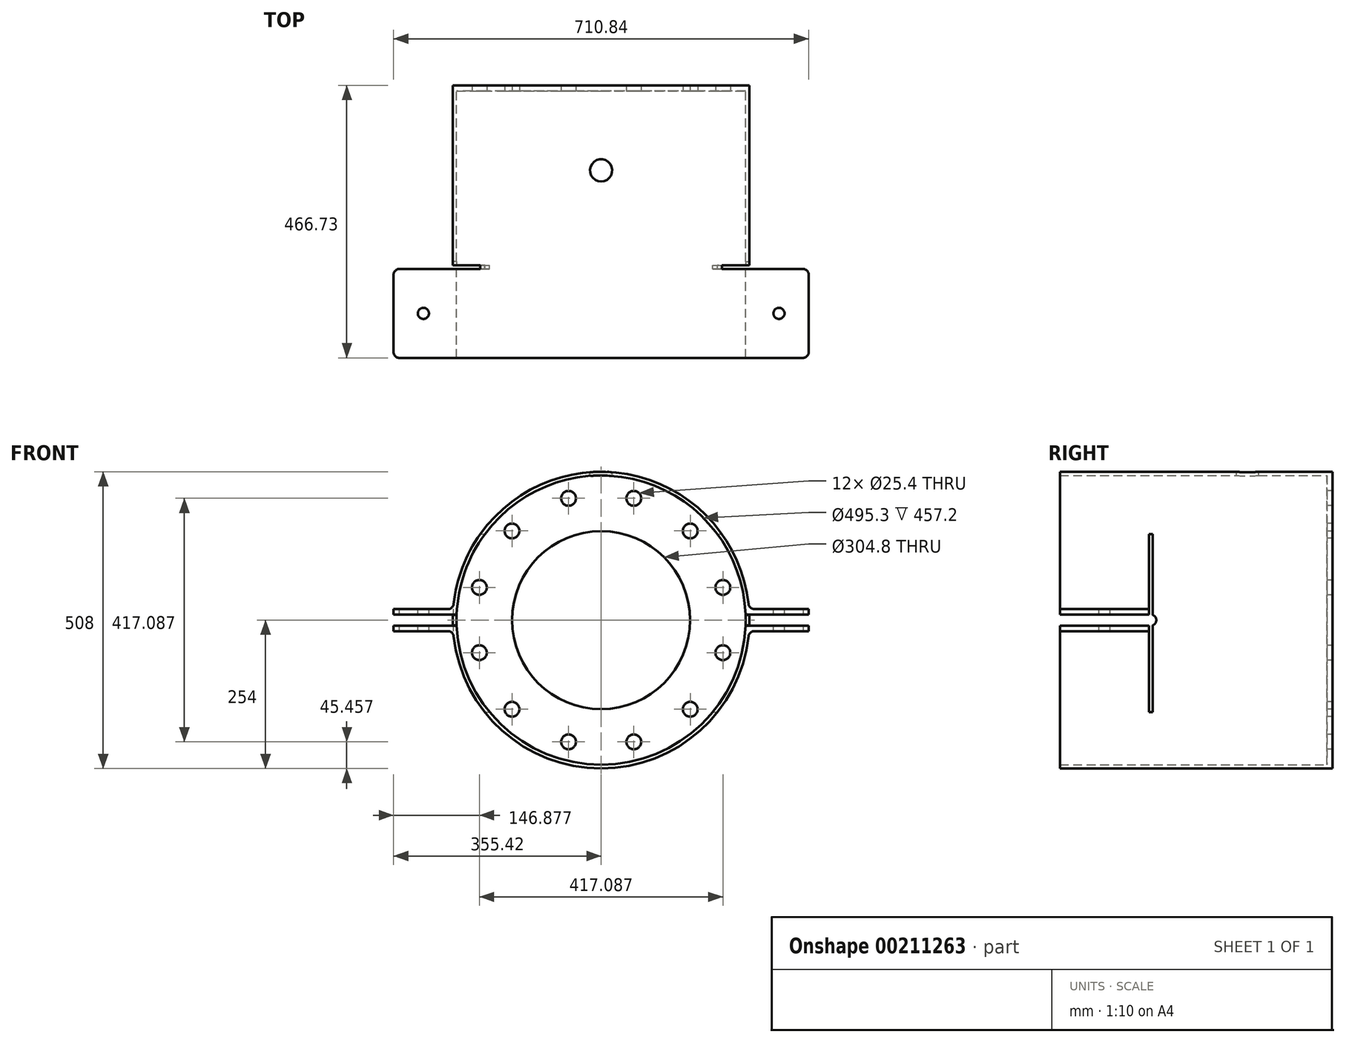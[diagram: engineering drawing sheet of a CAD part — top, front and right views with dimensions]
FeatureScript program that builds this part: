
annotation { "Feature Type Name" : "Feature", "Feature Type Description" : "" }
export const myFeature = defineFeature(function(context is Context, id is Id, definition is map)
    precondition{}
    {
        {
            var Q0;
            Q0=qCreatedBy(makeId("Front.planeOp"),FACE);
            var sketch = newSketch(context, id + "F0", { "sketchPlane" : qUnion([Q0])});
            skCircle(sketch, "E0", {"center": v(0, 0) * mm, "radius": 254 * mm});
            skCircle(sketch, "E1", {"center": v(0, 0) * mm, "radius": 247.65 * mm});
            skSolve(sketch);
        }
        {
            var Q0;
            Q0 = qSketchRegion(id + "F0", true);
            extrude(context, id + "F1", {"entities" : qUnion([Q0]), "depth" : 304.8 * mm});
        }
        {
            var Q0;
            Q0=makeQuery(id+"F1.opExtrude","CAP_FACE",FACE,{"disambiguationData":[OSD([sQuery(id+"F0.wireOp",EDGE,"E0"),sQuery(id+"F0.wireOp",EDGE,"E1")])],"isStart":false});
            var sketch = newSketch(context, id + "F2", { "sketchPlane" : qUnion([Q0])});
            skArc(sketch, "E2", {"start": v(253.82, -9.52) * mm, "mid": v(254, 0) * mm, "end": v(253.82, 9.53) * mm});
            skCircle(sketch, "E3", {"center": v(0, 0) * mm, "radius": 247.65 * mm});
            skLineSegment(sketch, "E4", {"start": v(-253.82, 9.53) * mm, "end": v(-355.42, 9.53) * mm});
            skLineSegment(sketch, "E5", {"start": v(-355.42, 9.53) * mm, "end": v(-355.42, 18.92) * mm});
            skLineSegment(sketch, "E6", {"start": v(-355.42, 18.92) * mm, "end": v(-253.3, 18.92) * mm});
            skLineSegment(sketch, "E7", {"start": v(-253.82, -9.52) * mm, "end": v(-355.42, -9.52) * mm});
            skLineSegment(sketch, "E8", {"start": v(-355.42, -9.52) * mm, "end": v(-355.42, -19.05) * mm});
            skLineSegment(sketch, "E9", {"start": v(-355.42, -19.05) * mm, "end": v(-253.28, -19.05) * mm});
            skLineSegment(sketch, "E10", {"start": v(253.82, 9.53) * mm, "end": v(355.42, 9.53) * mm});
            skLineSegment(sketch, "E11", {"start": v(355.42, 9.53) * mm, "end": v(355.42, 19.05) * mm});
            skLineSegment(sketch, "E12", {"start": v(355.42, 19.05) * mm, "end": v(253.28, 19.05) * mm});
            skLineSegment(sketch, "E13", {"start": v(253.82, -9.52) * mm, "end": v(355.42, -9.52) * mm});
            skLineSegment(sketch, "E14", {"start": v(355.42, -9.52) * mm, "end": v(355.42, -19.05) * mm});
            skLineSegment(sketch, "E15", {"start": v(355.42, -19.05) * mm, "end": v(253.28, -19.05) * mm});
            skArc(sketch, "E16.trimOffspring", {"start": v(253.28, 19.05) * mm, "mid": v(-0.06, 254) * mm, "end": v(-253.3, 18.92) * mm});
            skArc(sketch, "E17.trimOffspring", {"start": v(-253.82, 9.52) * mm, "mid": v(-254, 0) * mm, "end": v(-253.82, -9.53) * mm});
            skArc(sketch, "E18.trimOffspring", {"start": v(-253.28, -19.05) * mm, "mid": v(0, -254) * mm, "end": v(253.28, -19.05) * mm});
            skSolve(sketch);
        }
        {
            var Q0;
            Q0 = qSketchRegion(id + "F2", true);
            extrude(context, id + "F3", {"entities" : qUnion([Q0]), "operationType" : NewBodyOperationType.ADD, "depth" : 152.4 * mm});
        }
        {
            var Q0;
            Q0=makeQuery(id+"F3.opExtrude","CAP_FACE",FACE,{"disambiguationData":[OSD([sQuery(id+"F2.wireOp",EDGE,"E2"),sQuery(id+"F2.wireOp",EDGE,"E3"),sQuery(id+"F2.wireOp",EDGE,"E4"),sQuery(id+"F2.wireOp",EDGE,"E5"),sQuery(id+"F2.wireOp",EDGE,"E6"),sQuery(id+"F2.wireOp",EDGE,"E7"),sQuery(id+"F2.wireOp",EDGE,"E8"),sQuery(id+"F2.wireOp",EDGE,"E9"),sQuery(id+"F2.wireOp",EDGE,"E10"),sQuery(id+"F2.wireOp",EDGE,"E11"),sQuery(id+"F2.wireOp",EDGE,"E12"),sQuery(id+"F2.wireOp",EDGE,"E13"),sQuery(id+"F2.wireOp",EDGE,"E14"),sQuery(id+"F2.wireOp",EDGE,"E15"),sQuery(id+"F2.wireOp",EDGE,"E16.trimOffspring"),sQuery(id+"F2.wireOp",EDGE,"E17.trimOffspring"),sQuery(id+"F2.wireOp",EDGE,"E18.trimOffspring")])],"isStart":false});
            var sketch = newSketch(context, id + "F4", { "sketchPlane" : qUnion([Q0])});
            skLineSegment(sketch, "E19.bottom", {"start": v(-378.58, 9.53) * mm, "end": v(378.58, 9.53) * mm});
            skLineSegment(sketch, "E19.top", {"start": v(-378.58, -9.53) * mm, "end": v(378.58, -9.53) * mm});
            skLineSegment(sketch, "E19.left", {"start": v(-378.58, 9.53) * mm, "end": v(-378.58, -9.53) * mm});
            skLineSegment(sketch, "E19.right", {"start": v(378.58, 9.53) * mm, "end": v(378.58, -9.53) * mm});
            skPoint(sketch, "E19.middle", {"position": v(0, 0) * mm});
            skSolve(sketch);
        }
        {
            var Q0;
            Q0 = qSketchRegion(id + "F4", true);
            extrude(context, id + "F5", {"entities" : qUnion([Q0]), "operationType" : NewBodyOperationType.REMOVE, "oppositeDirection" : true, "depth" : 165.1 * mm});
        }
        {
            var Q0;
            {var subQ0=sQuery(id+"F4.wireOp",EDGE,"E19.bottom");Q0=makeQuery(id+"F5.boolean.opBoolean","COPY",EDGE,{"disambiguationData":[TD([makeQuery(id+"F3.opExtrude","SWEPT_FACE",FACE,{"disambiguationData":[OSD([sQuery(id+"F2.wireOp",EDGE,"E4")])]})])],"derivedFrom":makeQuery(id+"F5.opExtrude","CAP_EDGE",EDGE,{"disambiguationData":[OSD([subQ0])],"isStart":false})});}
            fillet(context, id + "F6", {"entities" : qUnion([Q0]), "radius" : 9.52 * mm, "tangentPropagation" : true, "allowEdgeOverflow" : false});
        }
        {
            var Q0;
            {var subQ0=sQuery(id+"F4.wireOp",EDGE,"E19.top");Q0=makeQuery(id+"F5.boolean.opBoolean","COPY",EDGE,{"disambiguationData":[TD([makeQuery(id+"F3.opExtrude","SWEPT_FACE",FACE,{"disambiguationData":[OSD([sQuery(id+"F2.wireOp",EDGE,"E7")])]})])],"derivedFrom":makeQuery(id+"F5.opExtrude","CAP_EDGE",EDGE,{"disambiguationData":[OSD([subQ0])],"isStart":false})});}
            var Q1;
            {var subQ0=sQuery(id+"F4.wireOp",EDGE,"E19.bottom");Q1=makeQuery(id+"F5.boolean.opBoolean","COPY",EDGE,{"disambiguationData":[TD([makeQuery(id+"F3.opExtrude","SWEPT_FACE",FACE,{"disambiguationData":[OSD([sQuery(id+"F2.wireOp",EDGE,"E10")])]})])],"derivedFrom":makeQuery(id+"F5.opExtrude","CAP_EDGE",EDGE,{"disambiguationData":[OSD([subQ0])],"isStart":false})});}
            var Q2;
            {var subQ0=sQuery(id+"F4.wireOp",EDGE,"E19.top");Q2=makeQuery(id+"F5.boolean.opBoolean","COPY",EDGE,{"disambiguationData":[TD([makeQuery(id+"F3.opExtrude","SWEPT_FACE",FACE,{"disambiguationData":[OSD([sQuery(id+"F2.wireOp",EDGE,"E13")])]})])],"derivedFrom":makeQuery(id+"F5.opExtrude","CAP_EDGE",EDGE,{"disambiguationData":[OSD([subQ0])],"isStart":false})});}
            fillet(context, id + "F7", {"entities" : qUnion([Q0, Q1, Q2]), "radius" : 9.52 * mm, "tangentPropagation" : true, "allowEdgeOverflow" : false});
        }
        {
            var Q0;
            Q0=makeQuery(id+"F3.opExtrude","SWEPT_FACE",FACE,{"disambiguationData":[OSD([sQuery(id+"F2.wireOp",EDGE,"E6")])]});
            var sketch = newSketch(context, id + "F8", { "sketchPlane" : qUnion([Q0])});
            skPoint(sketch, "E20.endSnap0", {"position": v(-253.3, -381) * mm});
            skCircle(sketch, "E21", {"center": v(-304.36, -381) * mm, "radius": 9.53 * mm});
            skSolve(sketch);
        }
        {
            var Q0;
            Q0 = qSketchRegion(id + "F8", true);
            extrude(context, id + "F9", {"entities" : qUnion([Q0]), "operationType" : NewBodyOperationType.REMOVE, "oppositeDirection" : true, "depth" : 76.2 * mm});
        }
        {
            var Q0;
            Q0=makeQuery(id+"F3.opExtrude","SWEPT_FACE",FACE,{"disambiguationData":[OSD([sQuery(id+"F2.wireOp",EDGE,"E12")])]});
            var sketch = newSketch(context, id + "F10", { "sketchPlane" : qUnion([Q0])});
            skCircle(sketch, "E22", {"center": v(304.62, -381) * mm, "radius": 9.53 * mm});
            skSolve(sketch);
        }
        {
            var Q0;
            Q0 = qSketchRegion(id + "F10", true);
            extrude(context, id + "F11", {"entities" : qUnion([Q0]), "operationType" : NewBodyOperationType.REMOVE, "oppositeDirection" : true, "depth" : 76.2 * mm});
        }
        {
            var Q0;
            Q0=makeQuery(id+"F3.opExtrude","SWEPT_EDGE",EDGE,{"disambiguationData":[OSD([sQuery(id+"F0.wireOp",EDGE,"E0"),sQuery(id+"F2.wireOp",EDGE,"E6"),sQuery(id+"F2.wireOp",EDGE,"E16.trimOffspring")])]});
            var Q1;
            Q1=makeQuery(id+"F3.opExtrude","SWEPT_EDGE",EDGE,{"disambiguationData":[OSD([sQuery(id+"F0.wireOp",EDGE,"E0"),sQuery(id+"F2.wireOp",EDGE,"E9"),sQuery(id+"F2.wireOp",EDGE,"E18.trimOffspring")])]});
            var Q2;
            Q2=makeQuery(id+"F3.opExtrude","SWEPT_EDGE",EDGE,{"disambiguationData":[OSD([sQuery(id+"F0.wireOp",EDGE,"E0"),sQuery(id+"F2.wireOp",EDGE,"E15"),sQuery(id+"F2.wireOp",EDGE,"E18.trimOffspring")])]});
            var Q3;
            Q3=makeQuery(id+"F3.opExtrude","SWEPT_EDGE",EDGE,{"disambiguationData":[OSD([sQuery(id+"F0.wireOp",EDGE,"E0"),sQuery(id+"F2.wireOp",EDGE,"E12"),sQuery(id+"F2.wireOp",EDGE,"E16.trimOffspring")])]});
            fillet(context, id + "F12", {"entities" : qUnion([Q0, Q1, Q2, Q3]), "radius" : 9.52 * mm, "tangentPropagation" : true, "allowEdgeOverflow" : false});
        }
        {
            var Q0;
            Q0=makeQuery(id+"F3.opExtrude","CAP_EDGE",EDGE,{"disambiguationData":[OSD([sQuery(id+"F2.wireOp",EDGE,"E14")])],"isStart":false});
            var Q1;
            Q1=makeQuery(id+"F3.opExtrude","CAP_EDGE",EDGE,{"disambiguationData":[OSD([sQuery(id+"F2.wireOp",EDGE,"E11")])],"isStart":false});
            var Q2;
            Q2=makeQuery(id+"F3.opExtrude","CAP_EDGE",EDGE,{"disambiguationData":[OSD([sQuery(id+"F2.wireOp",EDGE,"E14")])],"isStart":true});
            var Q3;
            Q3=makeQuery(id+"F3.opExtrude","CAP_EDGE",EDGE,{"disambiguationData":[OSD([sQuery(id+"F2.wireOp",EDGE,"E11")])],"isStart":true});
            var Q4;
            Q4=makeQuery(id+"F3.opExtrude","CAP_EDGE",EDGE,{"disambiguationData":[OSD([sQuery(id+"F2.wireOp",EDGE,"E5")])],"isStart":false});
            var Q5;
            Q5=makeQuery(id+"F3.opExtrude","CAP_EDGE",EDGE,{"disambiguationData":[OSD([sQuery(id+"F2.wireOp",EDGE,"E8")])],"isStart":false});
            var Q6;
            Q6=makeQuery(id+"F3.opExtrude","CAP_EDGE",EDGE,{"disambiguationData":[OSD([sQuery(id+"F2.wireOp",EDGE,"E5")])],"isStart":true});
            var Q7;
            Q7=makeQuery(id+"F3.opExtrude","CAP_EDGE",EDGE,{"disambiguationData":[OSD([sQuery(id+"F2.wireOp",EDGE,"E8")])],"isStart":true});
            fillet(context, id + "F13", {"entities" : qUnion([Q0, Q1, Q2, Q3, Q4, Q5, Q6, Q7]), "radius" : 9.52 * mm, "tangentPropagation" : true, "allowEdgeOverflow" : false});
        }
        {
            var Q0;
            Q0=makeQuery(id+"F1.opExtrude","CAP_FACE",FACE,{"disambiguationData":[OSD([sQuery(id+"F0.wireOp",EDGE,"E0"),sQuery(id+"F0.wireOp",EDGE,"E1")])],"isStart":true});
            var sketch = newSketch(context, id + "F14", { "sketchPlane" : qUnion([Q0])});
            skCircle(sketch, "E23", {"center": v(0, 0) * mm, "radius": 254 * mm});
            skCircle(sketch, "E24", {"center": v(0, 0) * mm, "radius": 152.4 * mm});
            skCircle(sketch, "E25", {"center": v(-55.88, -208.54) * mm, "radius": 12.7 * mm});
            skCircle(sketch, "E26.1.0", {"center": v(55.88, -208.54) * mm, "radius": 12.7 * mm});
            skCircle(sketch, "E26.2.0", {"center": v(152.66, -152.66) * mm, "radius": 12.7 * mm});
            skCircle(sketch, "E26.3.0", {"center": v(208.54, -55.88) * mm, "radius": 12.7 * mm});
            skCircle(sketch, "E26.4.0", {"center": v(208.54, 55.88) * mm, "radius": 12.7 * mm});
            skCircle(sketch, "E26.5.0", {"center": v(152.66, 152.66) * mm, "radius": 12.7 * mm});
            skCircle(sketch, "E26.6.0", {"center": v(55.88, 208.54) * mm, "radius": 12.7 * mm});
            skCircle(sketch, "E26.7.0", {"center": v(-55.88, 208.54) * mm, "radius": 12.7 * mm});
            skCircle(sketch, "E26.8.0", {"center": v(-152.66, 152.66) * mm, "radius": 12.7 * mm});
            skCircle(sketch, "E26.9.0", {"center": v(-208.54, 55.88) * mm, "radius": 12.7 * mm});
            skCircle(sketch, "E26.10.0", {"center": v(-208.54, -55.88) * mm, "radius": 12.7 * mm});
            skCircle(sketch, "E26.11.0", {"center": v(-152.66, -152.66) * mm, "radius": 12.7 * mm});
            skSolve(sketch);
        }
        {
            var Q0;
            Q0 = qSketchRegion(id + "F14", true);
            extrude(context, id + "F15", {"entities" : qUnion([Q0]), "operationType" : NewBodyOperationType.ADD, "depth" : 9.52 * mm});
        }
        {
            var Q0;
            Q0=qCreatedBy(makeId("Top.planeOp"),FACE);
            cPlane(context, id + "F16", {"entities" : qUnion([Q0]), "cplaneType" : CPlaneType.OFFSET, "offset" : 254 * mm, "width" : 152.4 * mm, "height" : 152.4 * mm});
        }
        {
            var Q0;
            Q0=qCreatedBy(id+"F16.planeOp",FACE);
            var sketch = newSketch(context, id + "F17", { "sketchPlane" : qUnion([Q0])});
            skCircle(sketch, "E27", {"center": v(0, -135.97) * mm, "radius": 19.05 * mm});
            skSolve(sketch);
        }
        {
            var Q0;
            Q0 = qSketchRegion(id + "F17", true);
            extrude(context, id + "F18", {"entities" : qUnion([Q0]), "operationType" : NewBodyOperationType.REMOVE, "oppositeDirection" : true, "depth" : 25.4 * mm});
        }
        {
            var Q0;
            Q0=makeQuery(id+"F3.opExtrude","SWEPT_FACE",FACE,{"disambiguationData":[OSD([sQuery(id+"F2.wireOp",EDGE,"E11")])]});
            var sketch = newSketch(context, id + "F19", { "sketchPlane" : qUnion([Q0])});
            skLineSegment(sketch, "E28", {"start": v(-304.81, -157.52) * mm, "end": v(-304.81, 147.28) * mm});
            skLineSegment(sketch, "E29", {"start": v(-304.81, 147.28) * mm, "end": v(-298.46, 147.28) * mm});
            skLineSegment(sketch, "E30", {"start": v(-298.46, 147.28) * mm, "end": v(-298.46, -157.52) * mm});
            skLineSegment(sketch, "E31", {"start": v(-298.46, -157.52) * mm, "end": v(-304.81, -157.52) * mm});
            skSolve(sketch);
        }
        {
            var Q0;
            Q0 = qSketchRegion(id + "F19", true);
            extrude(context, id + "F20", {"entities" : qUnion([Q0]), "operationType" : NewBodyOperationType.REMOVE, "endBound" : BoundingType.THROUGH_ALL, "oppositeDirection" : true, "depth" : 25.4 * mm});
        }
    });
